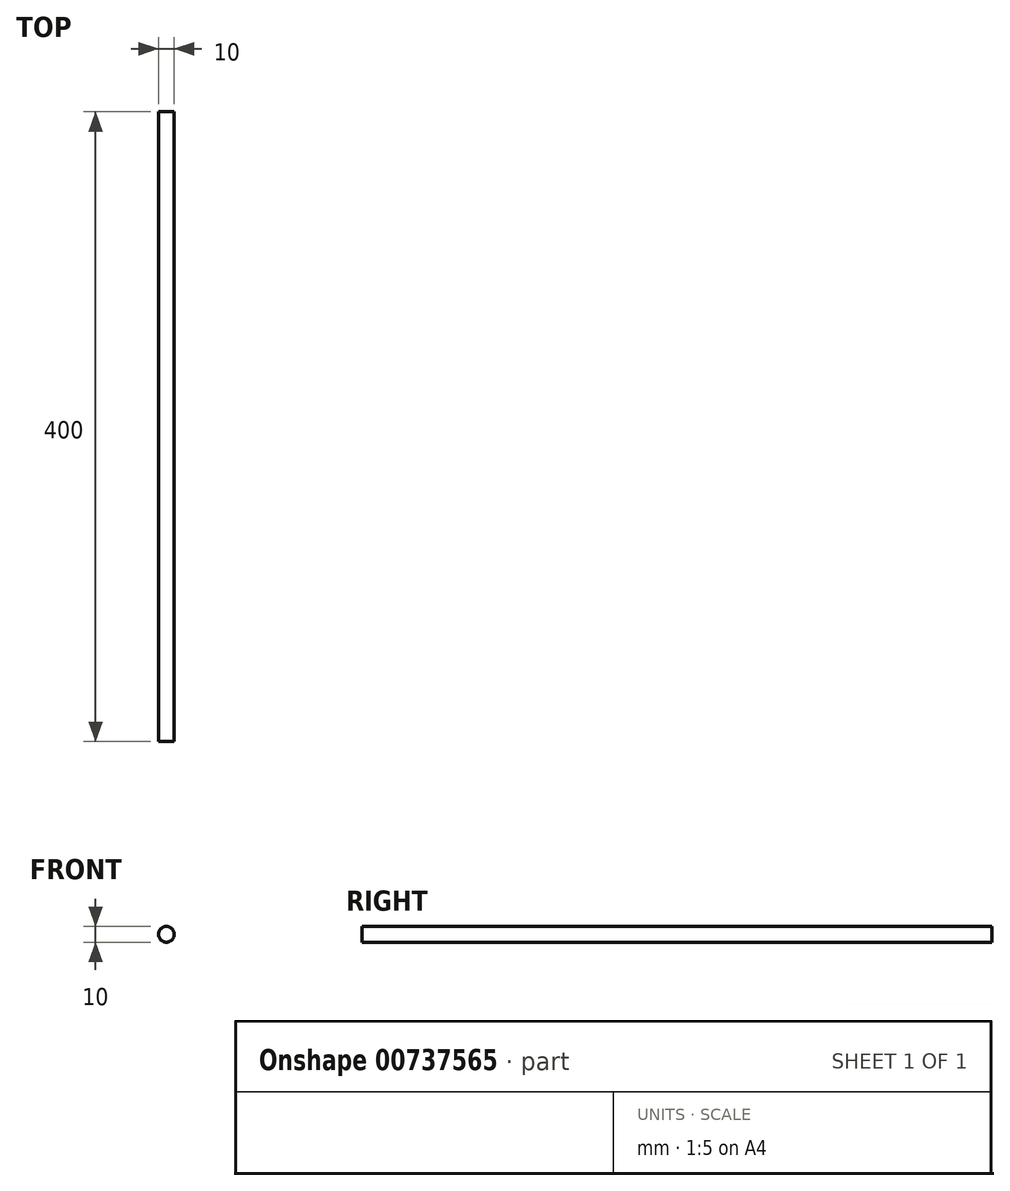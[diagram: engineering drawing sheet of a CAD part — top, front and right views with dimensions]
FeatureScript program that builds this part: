
annotation { "Feature Type Name" : "Feature", "Feature Type Description" : "" }
export const myFeature = defineFeature(function(context is Context, id is Id, definition is map)
    precondition{}
    {
        {
            var Q0;
            Q0=qCreatedBy(makeId("Front.planeOp"),FACE);
            var sketch = newSketch(context, id + "F0", { "sketchPlane" : qUnion([Q0])});
            skCircle(sketch, "E0", {"center": v(0, 0) * mm, "radius": 5 * mm});
            skSolve(sketch);
        }
        {
            var Q0;
            Q0 = qSketchRegion(id + "F0", true);
            extrude(context, id + "F1", {"entities" : qUnion([Q0]), "depth" : 400 * mm, "offsetDistance" : 25.4 * mm});
        }
    });
